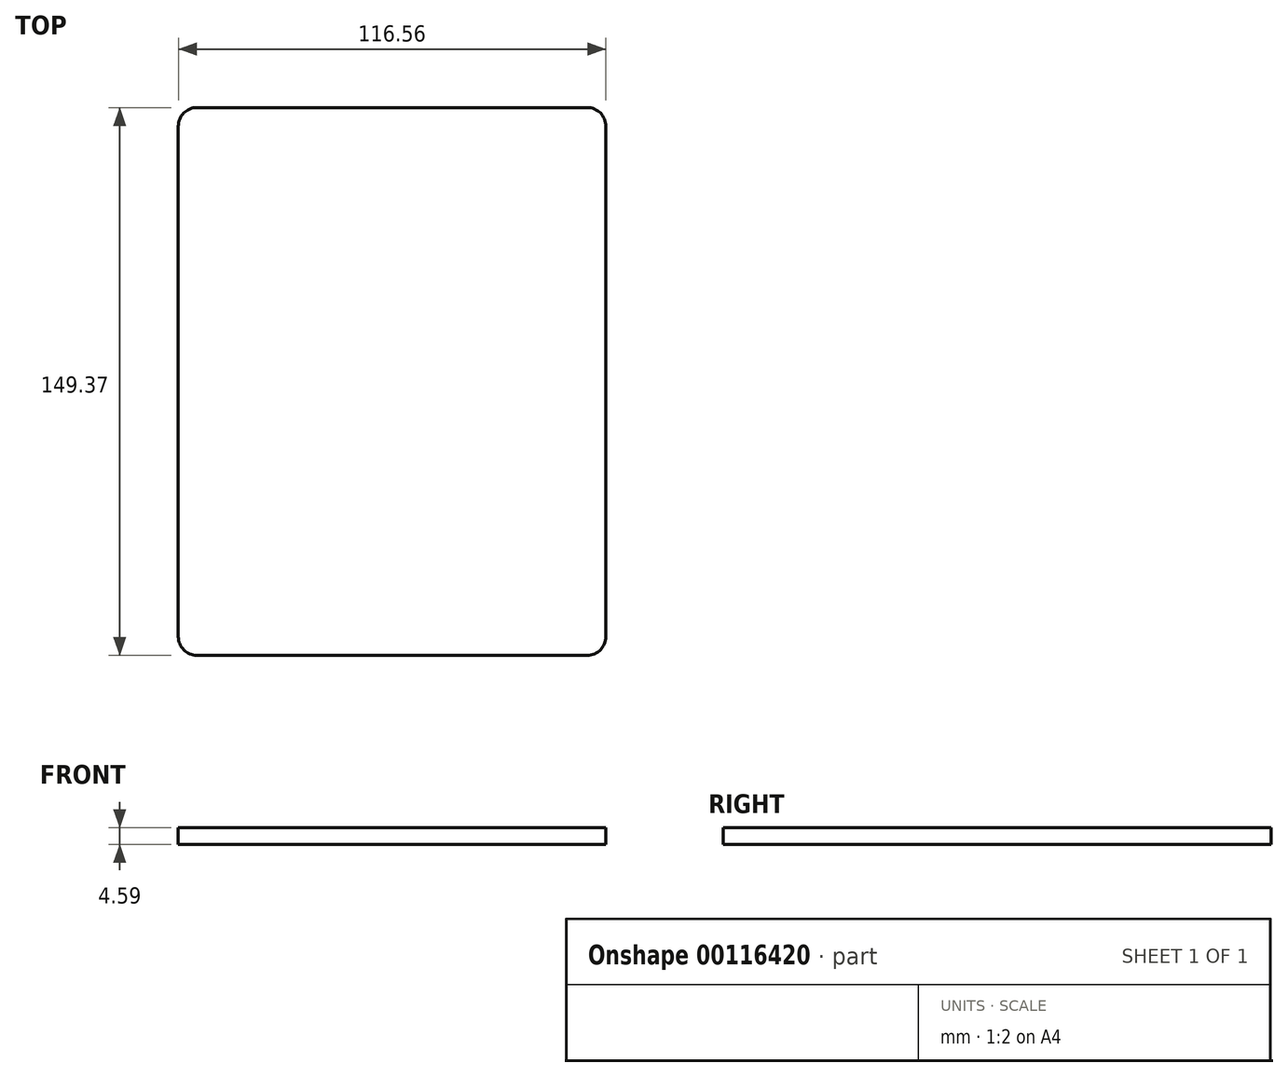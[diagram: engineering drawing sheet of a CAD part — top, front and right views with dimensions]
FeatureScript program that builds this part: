
annotation { "Feature Type Name" : "Feature", "Feature Type Description" : "" }
export const myFeature = defineFeature(function(context is Context, id is Id, definition is map)
    precondition{}
    {
        {
            var Q0;
            Q0=qCreatedBy(makeId("Top.planeOp"),FACE);
            var sketch = newSketch(context, id + "F0", { "sketchPlane" : qUnion([Q0])});
            skLineSegment(sketch, "E0.bottom", {"start": v(-58.3, 73.04) * mm, "end": v(58.27, 73.04) * mm});
            skLineSegment(sketch, "E0.top", {"start": v(-58.3, -76.33) * mm, "end": v(58.27, -76.33) * mm});
            skLineSegment(sketch, "E0.left", {"start": v(-58.3, 73.04) * mm, "end": v(-58.3, -76.33) * mm});
            skLineSegment(sketch, "E0.right", {"start": v(58.27, 73.04) * mm, "end": v(58.27, -76.33) * mm});
            skSolve(sketch);
        }
        {
            var Q0;
            Q0=makeQuery(id+"F0.imprint","IMPRINT",FACE,{"disambiguationData":[TD([[makeQuery(id+"F0.imprint","IMPRINT",EDGE,{"derivedFrom":sQuery(id+"F0.wireOp",EDGE,"E0.bottom")}),-1.0]])]});
            extrude(context, id + "F1", {"entities" : qUnion([Q0]), "depth" : 4.6 * mm});
        }
        {
            var Q0;
            Q0=makeQuery(id+"F1.opExtrude","SWEPT_EDGE",EDGE,{"disambiguationData":[OSD([sQuery(id+"F0.wireOp",EDGE,"E0.bottom"),sQuery(id+"F0.wireOp",EDGE,"E0.right")])]});
            fillet(context, id + "F2", {"entities" : qUnion([Q0]), "radius" : 5.08 * mm, "tangentPropagation" : true, "allowEdgeOverflow" : false});
        }
        {
            var Q0;
            Q0=makeQuery(id+"F1.opExtrude","SWEPT_EDGE",EDGE,{"disambiguationData":[OSD([sQuery(id+"F0.wireOp",EDGE,"E0.bottom"),sQuery(id+"F0.wireOp",EDGE,"E0.left")])]});
            fillet(context, id + "F3", {"entities" : qUnion([Q0]), "radius" : 5.08 * mm, "tangentPropagation" : true, "allowEdgeOverflow" : false});
        }
        {
            var Q0;
            Q0=makeQuery(id+"F1.opExtrude","SWEPT_EDGE",EDGE,{"disambiguationData":[OSD([sQuery(id+"F0.wireOp",EDGE,"E0.top"),sQuery(id+"F0.wireOp",EDGE,"E0.right")])]});
            var Q1;
            Q1=makeQuery(id+"F1.opExtrude","SWEPT_EDGE",EDGE,{"disambiguationData":[OSD([sQuery(id+"F0.wireOp",EDGE,"E0.top"),sQuery(id+"F0.wireOp",EDGE,"E0.left")])]});
            fillet(context, id + "F4", {"entities" : qUnion([Q0, Q1]), "radius" : 5.08 * mm, "tangentPropagation" : true, "allowEdgeOverflow" : false});
        }
    });
